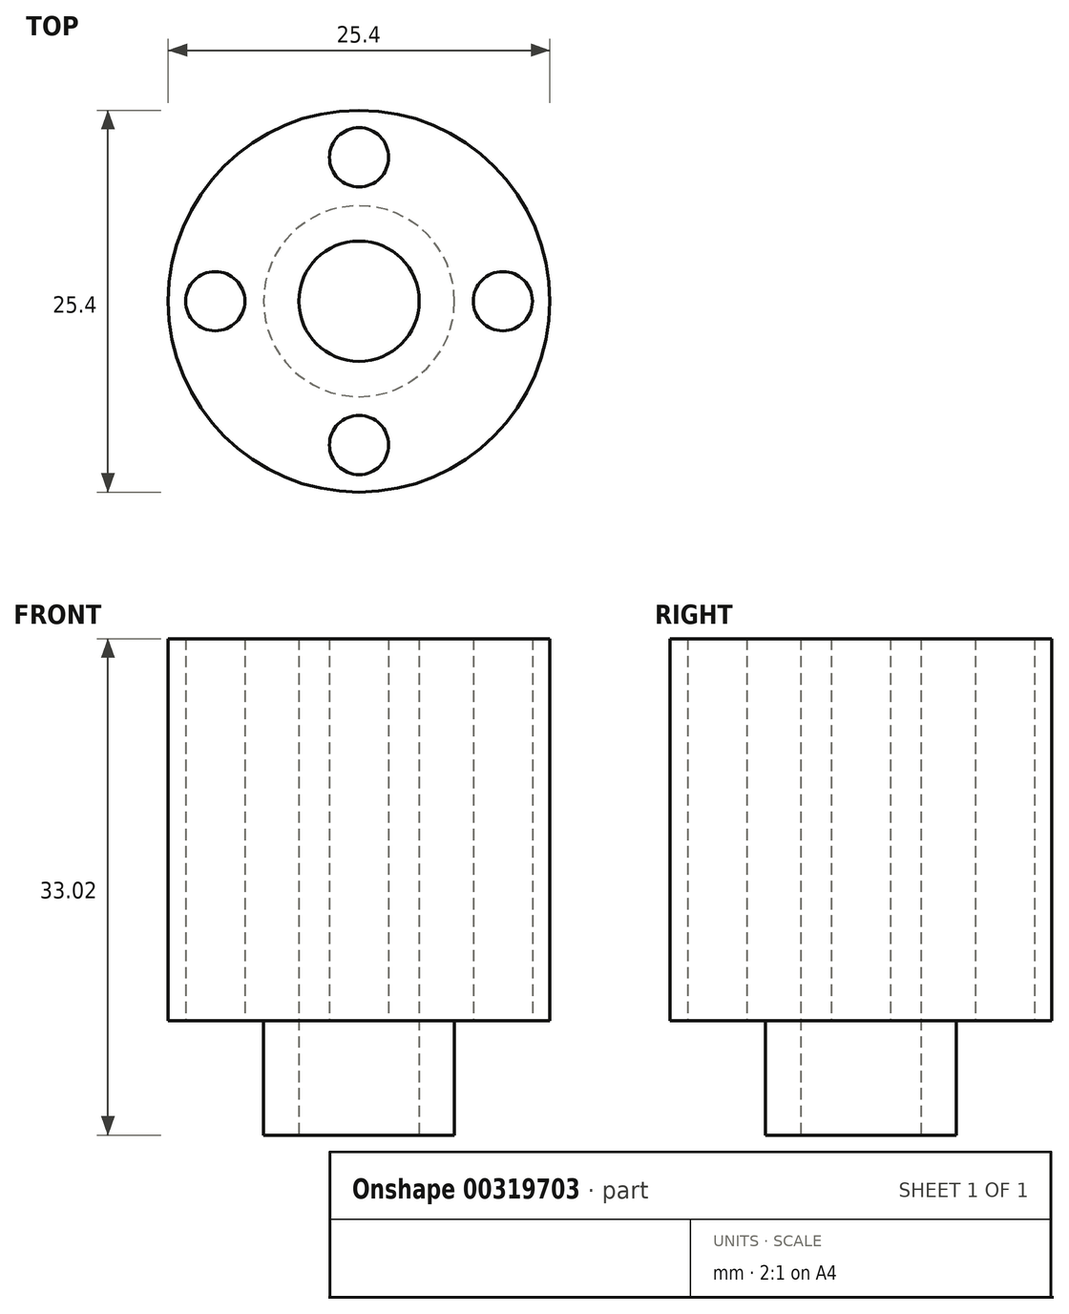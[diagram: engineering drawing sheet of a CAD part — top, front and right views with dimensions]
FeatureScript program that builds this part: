
annotation { "Feature Type Name" : "Feature", "Feature Type Description" : "" }
export const myFeature = defineFeature(function(context is Context, id is Id, definition is map)
    precondition{}
    {
        {
            var Q0;
            Q0=qCreatedBy(makeId("Top.planeOp"),FACE);
            var sketch = newSketch(context, id + "F0", { "sketchPlane" : qUnion([Q0])});
            skCircle(sketch, "E0", {"center": v(0, 0) * mm, "radius": 6.35 * mm});
            skCircle(sketch, "E1", {"center": v(0, 0) * mm, "radius": 12.7 * mm});
            skCircle(sketch, "E2", {"center": v(0, 0) * mm, "radius": 4 * mm});
            skCircle(sketch, "E3", {"center": v(0, 9.57) * mm, "radius": 1.97 * mm});
            skCircle(sketch, "E4.1.0", {"center": v(-9.57, 0) * mm, "radius": 1.97 * mm});
            skCircle(sketch, "E4.2.0", {"center": v(0, -9.57) * mm, "radius": 1.97 * mm});
            skCircle(sketch, "E4.3.0", {"center": v(9.57, 0) * mm, "radius": 1.97 * mm});
            skSolve(sketch);
        }
        {
            var Q0;
            Q0=makeQuery(id+"F0.imprint","IMPRINT",FACE,{"disambiguationData":[TD([[makeQuery(id+"F0.imprint","IMPRINT",EDGE,{"derivedFrom":sQuery(id+"F0.wireOp",EDGE,"E0")}),1.0]])]});
            var Q1;
            Q1=makeQuery(id+"F0.imprint","IMPRINT",FACE,{"disambiguationData":[TD([[makeQuery(id+"F0.imprint","IMPRINT",EDGE,{"derivedFrom":sQuery(id+"F0.wireOp",EDGE,"E0")}),-1.0]])]});
            extrude(context, id + "F1", {"entities" : qUnion([Q0, Q1]), "depth" : 25.4 * mm});
        }
        {
            var Q0;
            Q0=makeQuery(id+"F0.imprint","IMPRINT",FACE,{"disambiguationData":[TD([[makeQuery(id+"F0.imprint","IMPRINT",EDGE,{"derivedFrom":sQuery(id+"F0.wireOp",EDGE,"E0")}),1.0]])]});
            extrude(context, id + "F2", {"entities" : qUnion([Q0]), "operationType" : NewBodyOperationType.ADD, "oppositeDirection" : true, "depth" : 7.62 * mm});
        }
    });
